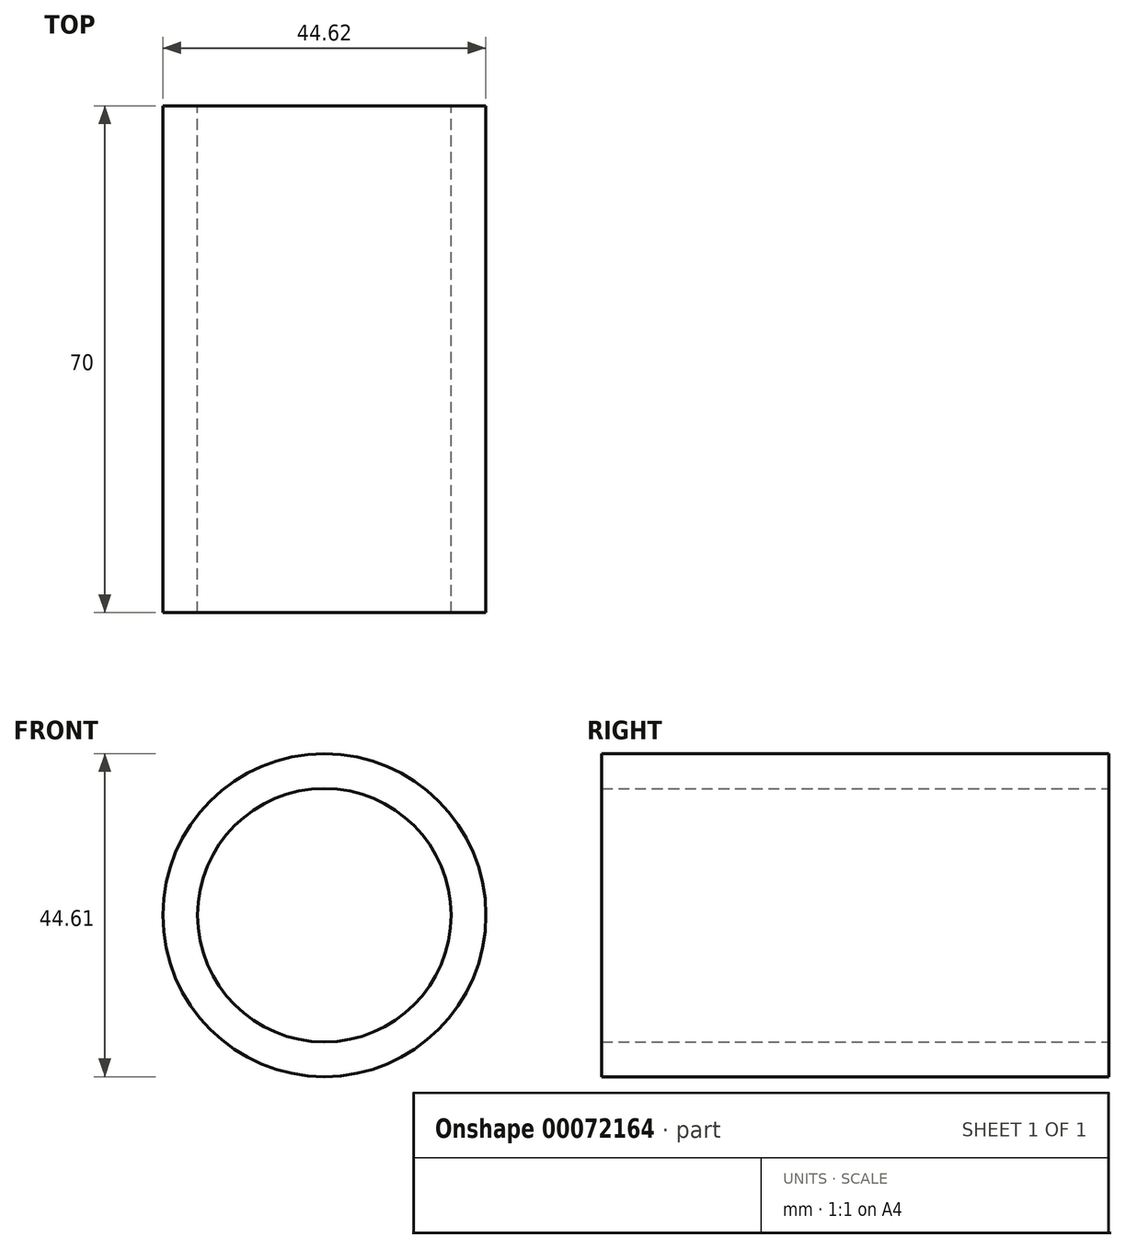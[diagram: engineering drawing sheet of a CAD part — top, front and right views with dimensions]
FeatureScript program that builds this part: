
annotation { "Feature Type Name" : "Feature", "Feature Type Description" : "" }
export const myFeature = defineFeature(function(context is Context, id is Id, definition is map)
    precondition{}
    {
        {
            var Q0;
            Q0=qCreatedBy(makeId("Front.planeOp"),FACE);
            var sketch = newSketch(context, id + "F0", { "sketchPlane" : qUnion([Q0])});
            skCircle(sketch, "E0", {"center": v(-46.4, 32.38) * mm, "radius": 22.3 * mm});
            skCircle(sketch, "E1", {"center": v(-46.4, 32.38) * mm, "radius": 17.5 * mm});
            skSolve(sketch);
        }
        {
            var Q0;
            Q0=makeQuery(id+"F0.imprint","IMPRINT",FACE,{"disambiguationData":[TD([[makeQuery(id+"F0.imprint","IMPRINT",EDGE,{"derivedFrom":sQuery(id+"F0.wireOp",EDGE,"E0")}),1.0]])]});
            extrude(context, id + "F1", {"entities" : qUnion([Q0]), "depth" : 70 * mm});
        }
    });
